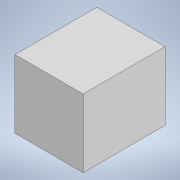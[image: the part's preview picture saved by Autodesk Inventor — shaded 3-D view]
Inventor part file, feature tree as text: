
AUTODESK INVENTOR PART (.ipt)
format: ipt  version: 2021 (Build 250183000, 183)  size: 122,368 bytes
history: native  units: mm
features: extrude x3, sketch x3, chamfer x1
ambient origin geometry x8: Origin, YZ Plane, XZ Plane, XY Plane, X Axis, Y Axis, Z Axis, Center Point
bodies: Solid1 (feature_tree)
feature tree (7):
  extrude  "Extrusion1"  Depth=25.0mm
  extrude  "Extrusion2"  Depth=25.0mm
  chamfer  "Chamfer1"  Distance=15.0mm
  extrude  "Extrusion3"  Depth=15.0mm
  sketch  "Sketch2"  dims[d0=15.0mm d1=25.0mm]
  sketch  "Sketch3"  dims[d2=25.0mm d3=12.5mm]
  sketch  "Sketch4"  dims[d4=12.5mm d5=15.0mm d6=15.0mm d7=25.0mm d8=0.0mm d9=15.0mm d10=12.0mm d11=5.0mm d12=0.0mm d13=1.5mm d14=2.0mm d15=45.0deg d16=5.0mm d17=0.0mm]
